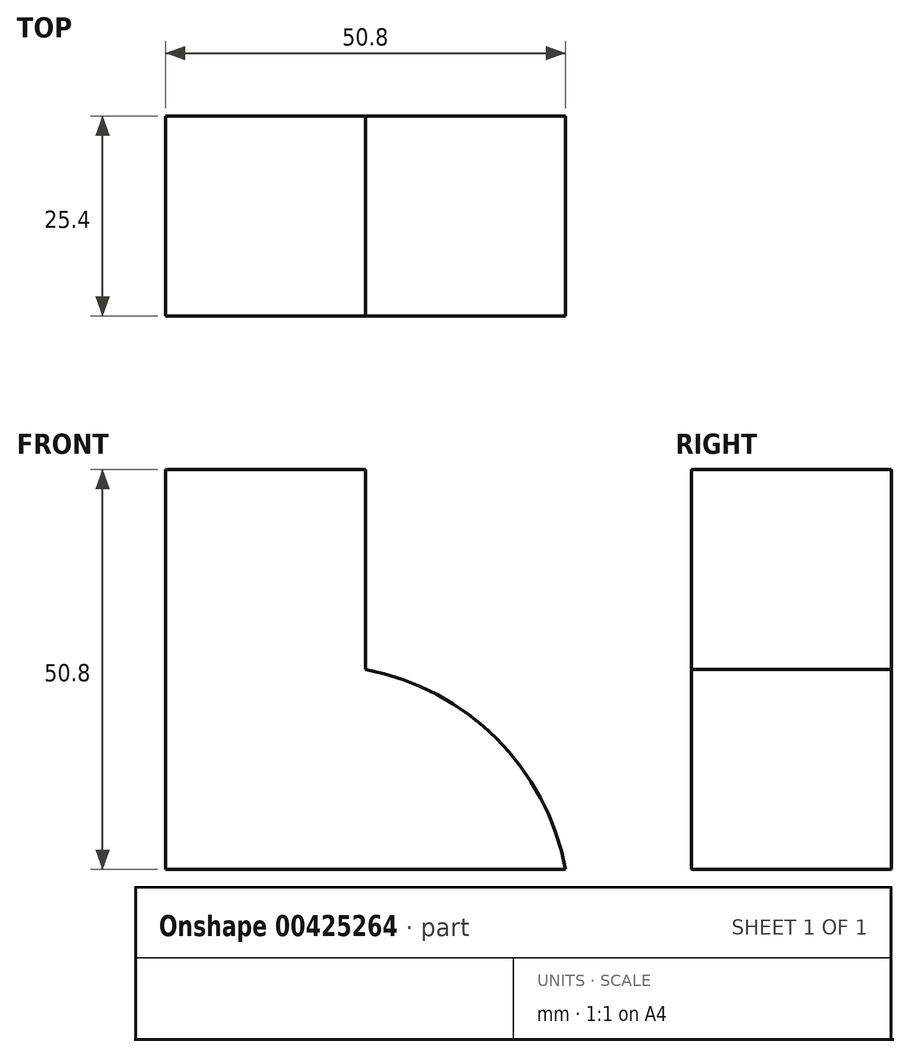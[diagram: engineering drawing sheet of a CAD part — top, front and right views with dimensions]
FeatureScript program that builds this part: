
annotation { "Feature Type Name" : "Feature", "Feature Type Description" : "" }
export const myFeature = defineFeature(function(context is Context, id is Id, definition is map)
    precondition{}
    {
        {
            var Q0;
            Q0=qCreatedBy(makeId("Front.planeOp"),FACE);
            var sketch = newSketch(context, id + "F0", { "sketchPlane" : qUnion([Q0])});
            skLineSegment(sketch, "E0", {"start": v(-37.24, -8.97) * mm, "end": v(-37.24, 41.83) * mm});
            skLineSegment(sketch, "E1", {"start": v(-37.24, -8.97) * mm, "end": v(13.56, -8.97) * mm});
            skLineSegment(sketch, "E2", {"start": v(-37.24, 41.83) * mm, "end": v(-11.84, 41.83) * mm});
            skLineSegment(sketch, "E3", {"start": v(-11.84, 41.83) * mm, "end": v(-11.84, 16.42) * mm});
            skArc(sketch, "E4", {"start": v(13.56, -8.97) * mm, "mid": v(4.8, 7.67) * mm, "end": v(-11.84, 16.42) * mm});
            skSolve(sketch);
        }
        {
            var Q0;
            Q0=makeQuery(id+"F0.imprint","IMPRINT",FACE,{"disambiguationData":[TD([[makeQuery(id+"F0.imprint","IMPRINT",EDGE,{"derivedFrom":sQuery(id+"F0.wireOp",EDGE,"E0")}),-1.0]])]});
            extrude(context, id + "F1", {"entities" : qUnion([Q0]), "depth" : 25.4 * mm});
        }
    });
